# Revit family: Domotics-DomesticRanges-GEWISS-27COMBI_SYSTEM-IP40_3P+3P_4P+4P_HORIZONTAL
name_source: partatom
category: Apparecchi elettrici
revit_build: Autodesk Revit 2016 (Build: 20161004_0715(x64)
units: mm (PartAtom-declared; Revit-internal decimal feet)

## family parameters
Condiviso = No
Host = Superficie
Mantenere orientamento annotazione = No
Numero OmniClass = 23.80.30.14.24
Punto di calcolo locali = No
Quota connettore circolare = Usa diametro
Taglio con vuoti quando caricato = Sì
Tipo di parte = Normale
Titolo OmniClass = Junction Boxes

## types (1)
- Domotics-DomesticRanges-GEWISS-27COMBI_SYSTEM-IP40_3P+3P_4P+4P_HORIZONTAL
    Bidimensionale = bidimensionale system contenitori IP40 2PH : 4P
    Catalogue = DOMOTICS
    Catalogue Range = 27COMBI
    Characteristics = Halogen free
    Colour = Grey RAL 7035
    Compartment pre-arrangement = 2
    Configuration = Module 4 x 2
    Description: = 8 gang
    Descrizione = HORIZ.8(2X4) GANG ENCLOSURE IP40
    Dimensions LxHxD (mm) = 231x82x55
    EAN code = 8011564055292
    Electrocod = 0212
    Glow Wire Test = 650°C
    IDF = c6da763c-a52e-46d9-8fa2-83b686df08e0
    IDT = 6f7883e7-52d8-43d5-a5dc-da2a76c29509
    IP degree = IP40
    Immagine tipo = GW27006.jpg
    Installation temperature = -25 +60 °C
    Insulation class = II
    Larghezza scatola = 231 mm  [stored 0.757874 ft]
    Lid screws = Corrosion-resistant steel
    Modello = GW27006
    No. knockout holes Ã˜ 23 = 10
    No. knockout holes Ã˜23 = 10 on sides / 2 on the bottom
    Outer dim. LxHxD (mm) = 231x82x55
    Produttore = GEWISS S.p.A.
    Prospetto di default = 1219 mm
    SCATOLA = GEWISS GRIGIO
    SEO = Enclosure
    Shock resistance = IK07
    Standard; = EN 60670-1
    Technical sheet = https://www.gewiss.com
    Thermo-pressure with ball = 70
    Tipo = SYSTEM CONTENITORI IP40 2P H_BASE : GW27006 - 4x2 posti orizzontali
    Torque screws tightening = 0,8NM
    Type of knockout holes = Removable with tool
    URL = https://www.gewiss.com
    Version file RFA = 19.4

note: source unit labels omitted for Thermo-pressure with ball — the stored unit's dimension contradicts the parameter name (converter mislabeling)

note: [stored X ft] marks values corroborated as IEEE doubles in the binary element streams (Revit-internal decimal feet)

## geometry (parser evidence)
native form markers: Blend x2
no freeform markers — native parametric forms only
